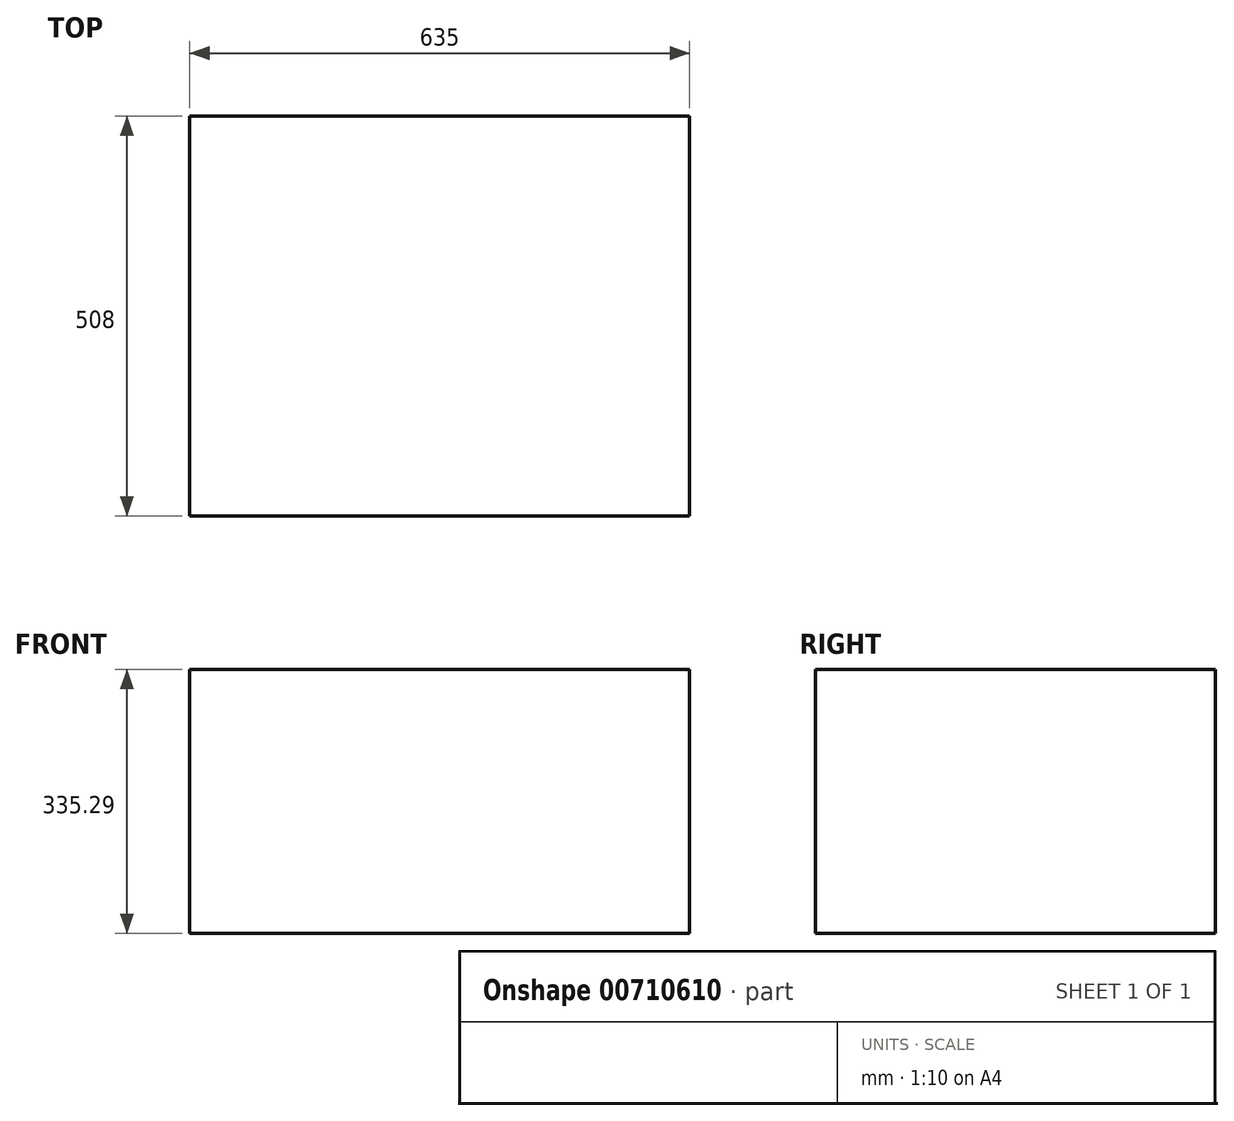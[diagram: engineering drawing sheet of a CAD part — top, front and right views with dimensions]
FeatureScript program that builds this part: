
annotation { "Feature Type Name" : "Feature", "Feature Type Description" : "" }
export const myFeature = defineFeature(function(context is Context, id is Id, definition is map)
    precondition{}
    {
        {
            var Q0;
            Q0=qCreatedBy(makeId("Front.planeOp"),FACE);
            var sketch = newSketch(context, id + "F0", { "sketchPlane" : qUnion([Q0])});
            skLineSegment(sketch, "E0.bottom", {"start": v(0, 0) * mm, "end": v(635, 0) * mm});
            skLineSegment(sketch, "E0.top", {"start": v(0, -335.3) * mm, "end": v(635, -335.3) * mm});
            skLineSegment(sketch, "E0.left", {"start": v(0, 0) * mm, "end": v(0, -335.3) * mm});
            skLineSegment(sketch, "E0.right", {"start": v(635, 0) * mm, "end": v(635, -335.3) * mm});
            skSolve(sketch);
        }
        {
            var Q0;
            Q0 = qSketchRegion(id + "F0", true);
            extrude(context, id + "F1", {"entities" : qUnion([Q0]), "depth" : 508 * mm, "offsetDistance" : 25.4 * mm});
        }
    });
